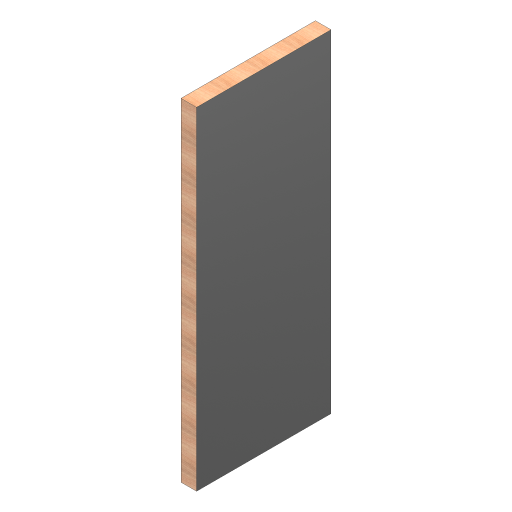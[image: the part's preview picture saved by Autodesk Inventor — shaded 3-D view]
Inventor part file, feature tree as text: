
AUTODESK INVENTOR PART (.ipt)
format: ipt  version: 2023 (Build 270158000, 158)  size: 249,344 bytes
history: native  units: mm
features: extrude x1, sketch x1
ambient origin geometry x8: Origin, YZ Plane, XZ Plane, XY Plane, X Axis, Y Axis, Z Axis, Center Point
bodies: 实体1 (feature_tree)
feature tree (2):
  extrude  "拉伸1"  Depth=950.0mm
  sketch  "草图1"  dims[d0=2350.0mm d1=950.0mm d2=110.0mm d3=0.0mm]
